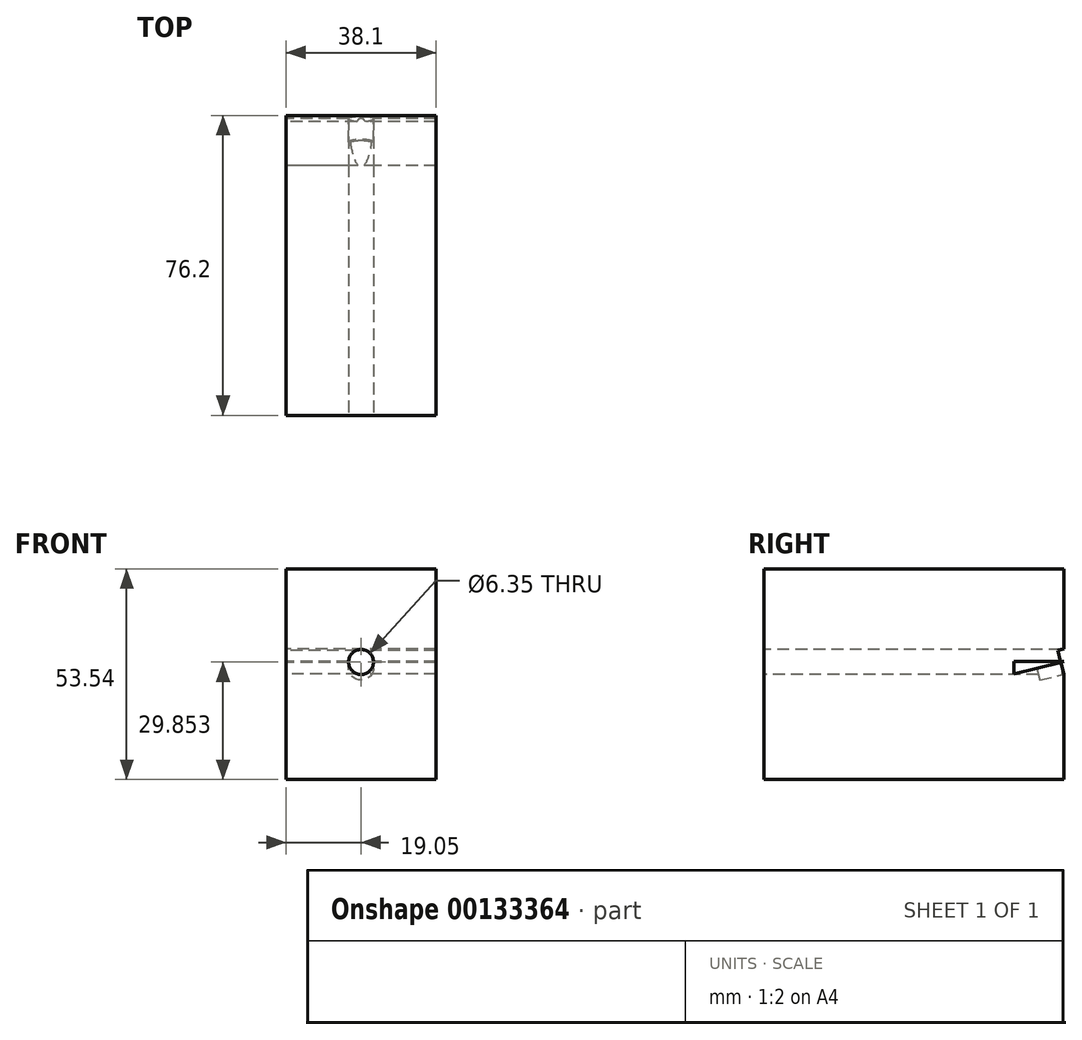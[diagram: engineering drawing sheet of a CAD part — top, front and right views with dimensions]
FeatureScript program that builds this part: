
annotation { "Feature Type Name" : "Feature", "Feature Type Description" : "" }
export const myFeature = defineFeature(function(context is Context, id is Id, definition is map)
    precondition{}
    {
        {
            var Q0;
            Q0=qCreatedBy(makeId("Right.planeOp"),FACE);
            var sketch = newSketch(context, id + "F0", { "sketchPlane" : qUnion([Q0])});
            skLineSegment(sketch, "E0.bottom", {"start": v(-38.1, 26.77) * mm, "end": v(38.1, 26.77) * mm});
            skLineSegment(sketch, "E0.top", {"start": v(-38.1, -26.77) * mm, "end": v(38.1, -26.77) * mm});
            skLineSegment(sketch, "E0.left", {"start": v(-38.1, 26.77) * mm, "end": v(-38.1, -26.77) * mm});
            skLineSegment(sketch, "E0.right", {"start": v(38.1, 26.77) * mm, "end": v(38.1, -26.77) * mm});
            skPoint(sketch, "E0.middle", {"position": v(0, 0) * mm});
            skPoint(sketch, "E1.oppositeSnap0", {"position": v(38.1, 0) * mm});
            skLineSegment(sketch, "E1.bottom", {"start": v(38.1, 3.18) * mm, "end": v(25.4, 3.18) * mm});
            skLineSegment(sketch, "E1.top", {"start": v(38.1, 0) * mm, "end": v(25.4, 0) * mm});
            skLineSegment(sketch, "E1.left", {"start": v(38.1, 3.17) * mm, "end": v(38.1, 0) * mm});
            skLineSegment(sketch, "E1.right", {"start": v(25.4, 3.17) * mm, "end": v(25.4, 0) * mm});
            skLineSegment(sketch, "E2", {"start": v(38.1, 3.17) * mm, "end": v(25.4, 0) * mm, "construction": true});
            skLineSegment(sketch, "E3", {"start": v(38.1, 0) * mm, "end": v(37.35, 2.99) * mm, "construction": true});
            skLineSegment(sketch, "E4", {"start": v(37.35, 2.99) * mm, "end": v(36.71, 5.55) * mm, "construction": true});
            skPoint(sketch, "E5", {"position": v(36.58, 6.07) * mm});
            skPoint(sketch, "E6", {"position": v(38.12, -0.1) * mm});
            skLineSegment(sketch, "E7", {"start": v(36.58, 6.07) * mm, "end": v(38.1, 6.45) * mm});
            skLineSegment(sketch, "E8", {"start": v(38.1, 6.45) * mm, "end": v(25.4, 3.27) * mm});
            skLineSegment(sketch, "E9", {"start": v(38.12, -0.1) * mm, "end": v(25.4, -3.27) * mm});
            skLineSegment(sketch, "E10", {"start": v(25.4, -3.27) * mm, "end": v(25.4, 3.17) * mm});
            skLineSegment(sketch, "E11", {"start": v(25.4, 0) * mm, "end": v(38.1, 3.18) * mm});
            skLineSegment(sketch, "E12", {"start": v(36.58, 6.07) * mm, "end": v(38.12, -0.1) * mm});
            skPoint(sketch, "E13", {"position": v(38.1, -1.62) * mm});
            skLineSegment(sketch, "E14", {"start": v(38.1, -1.62) * mm, "end": v(32.03, -1.62) * mm});
            skLineSegment(sketch, "E15", {"start": v(38.12, -0.1) * mm, "end": v(59.7, -0.1) * mm});
            skLineSegment(sketch, "E16", {"start": v(59.7, -0.1) * mm, "end": v(59.7, -1.62) * mm});
            skLineSegment(sketch, "E17", {"start": v(59.7, -1.62) * mm, "end": v(38.1, -1.62) * mm});
            skSolve(sketch);
        }
        {
            var Q0;
            Q0=makeQuery(id+"F0.imprint","IMPRINT",FACE,{"disambiguationData":[TD([[makeQuery(id+"F0.imprint","IMPRINT",EDGE,{"derivedFrom":sQuery(id+"F0.wireOp",EDGE,"E0.bottom")}),-1.0]])]});
            var Q1;
            {var subQ0=sQuery(id+"F0.wireOp",EDGE,"E10");var subQ1=sQuery(id+"F0.wireOp",EDGE,"E1.bottom");var subQ2=makeQuery(id+"F0.imprint","INTERSECT",VERTEX,{"derivedFrom":[subQ1,subQ0]});Q1=makeQuery(id+"F0.imprint","IMPRINT",FACE,{"disambiguationData":[TD([[makeQuery(id+"F0.imprint","IMPRINT",EDGE,{"disambiguationData":[TD([[subQ2,1.0]])],"derivedFrom":subQ1}),1.0]])]});}
            var Q2;
            {var subQ0=sQuery(id+"F0.wireOp",EDGE,"E1.top");Q2=makeQuery(id+"F0.imprint","IMPRINT",FACE,{"disambiguationData":[TD([[makeQuery(id+"F0.imprint","IMPRINT",EDGE,{"derivedFrom":subQ0}),-1.0]])]});}
            var Q3;
            {var subQ0=sQuery(id+"F0.wireOp",EDGE,"E1.top");Q3=makeQuery(id+"F0.imprint","IMPRINT",FACE,{"disambiguationData":[TD([[makeQuery(id+"F0.imprint","IMPRINT",EDGE,{"derivedFrom":subQ0}),1.0]])]});}
            var Q4;
            {var subQ0=sQuery(id+"F0.wireOp",EDGE,"E14");Q4=makeQuery(id+"F0.imprint","IMPRINT",FACE,{"disambiguationData":[TD([[makeQuery(id+"F0.imprint","IMPRINT",EDGE,{"derivedFrom":subQ0}),-1.0]])]});}
            extrude(context, id + "F1", {"entities" : qUnion([Q0, Q1, Q2, Q3, Q4]), "endBound" : BoundingType.SYMMETRIC, "depth" : 38.1 * mm});
        }
        {
            var Q0;
            Q0=makeQuery(id+"F1.opExtrude","SWEPT_FACE",FACE,{"disambiguationData":[OSD([sQuery(id+"F0.wireOp",EDGE,"E12")])]});
            var sketch = newSketch(context, id + "F2", { "sketchPlane" : qUnion([Q0])});
            skPoint(sketch, "E18", {"position": v(0, -6.07) * mm});
            skPoint(sketch, "E18.positionSnap0", {"position": v(0, -9.24) * mm});
            skCircle(sketch, "E19", {"center": v(0, -6.07) * mm, "radius": 3.18 * mm});
            skSolve(sketch);
        }
        {
            var Q0;
            {var subQ0=sQuery(id+"F2.wireOp",EDGE,"E19");var subQ1=sQuery(id+"F0.wireOp",EDGE,"E12");var subQ2=makeQuery(id+"F1.opExtrude","SWEPT_EDGE",EDGE,{"disambiguationData":[OSD([sQuery(id+"F0.wireOp",EDGE,"E8"),subQ1])]});var subQ3=makeQuery(id+"F2.imprint","INTERSECT",VERTEX,{"disambiguationData":[OD(0.0)],"derivedFrom":[subQ2,subQ0]});Q0=makeQuery(id+"F2.imprint","IMPRINT",FACE,{"disambiguationData":[TD([[makeQuery(id+"F2.imprint","IMPRINT",EDGE,{"disambiguationData":[TD([[subQ3,-1.0]])],"derivedFrom":subQ2}),-1.0]])]});}
            extrude(context, id + "F3", {"entities" : qUnion([Q0]), "operationType" : NewBodyOperationType.REMOVE, "oppositeDirection" : true, "depth" : 6.27 * mm});
        }
        {
            var Q0;
            {var subQ1=sQuery(id+"F0.wireOp",EDGE,"E0.right");var subQ3=sQuery(id+"F0.wireOp",EDGE,"E8");var subQ4=makeQuery(id+"F0.imprint","INTERSECT",VERTEX,{"derivedFrom":[subQ1,subQ3]});Q0=makeQuery(id+"F0.imprint","IMPRINT",FACE,{"disambiguationData":[TD([[makeQuery(id+"F0.imprint","IMPRINT",EDGE,{"disambiguationData":[TD([[subQ4,-1.0]])],"derivedFrom":subQ3}),1.0]])]});}
            var Q1;
            {var subQ0=sQuery(id+"F0.wireOp",EDGE,"E1.left");Q1=makeQuery(id+"F0.imprint","IMPRINT",FACE,{"disambiguationData":[TD([[makeQuery(id+"F0.imprint","IMPRINT",EDGE,{"derivedFrom":subQ0}),-1.0]])]});}
            var Q2;
            {var subQ1=sQuery(id+"F0.wireOp",EDGE,"E1.bottom");var subQ3=sQuery(id+"F0.wireOp",EDGE,"E12");var subQ4=makeQuery(id+"F0.imprint","INTERSECT",VERTEX,{"derivedFrom":[subQ1,subQ3]});Q2=makeQuery(id+"F0.imprint","IMPRINT",FACE,{"disambiguationData":[TD([[makeQuery(id+"F0.imprint","IMPRINT",EDGE,{"disambiguationData":[TD([[subQ4,-1.0]])],"derivedFrom":subQ3}),1.0]])]});}
            extrude(context, id + "F4", {"entities" : qUnion([Q0, Q1, Q2]), "endBound" : BoundingType.SYMMETRIC, "depth" : 38.1 * mm});
        }
        {
            var Q0;
            Q0=makeQuery(id+"F1.opExtrude","SWEPT_FACE",FACE,{"disambiguationData":[OSD([sQuery(id+"F0.wireOp",EDGE,"E0.left")])]});
            var sketch = newSketch(context, id + "F5", { "sketchPlane" : qUnion([Q0])});
            skPoint(sketch, "E20", {"position": v(0, 3.08) * mm});
            skCircle(sketch, "E21", {"center": v(0, 3.08) * mm, "radius": 3.18 * mm});
            skSolve(sketch);
        }
        {
            var Q0;
            Q0=makeQuery(id+"F5.imprint","IMPRINT",FACE,{"disambiguationData":[TD([[makeQuery(id+"F5.imprint","IMPRINT",EDGE,{"derivedFrom":sQuery(id+"F5.wireOp",EDGE,"E21")}),1.0]])]});
            extrude(context, id + "F6", {"entities" : qUnion([Q0]), "operationType" : NewBodyOperationType.REMOVE, "endBound" : BoundingType.THROUGH_ALL, "oppositeDirection" : true, "depth" : 25.4 * mm});
        }
    });
